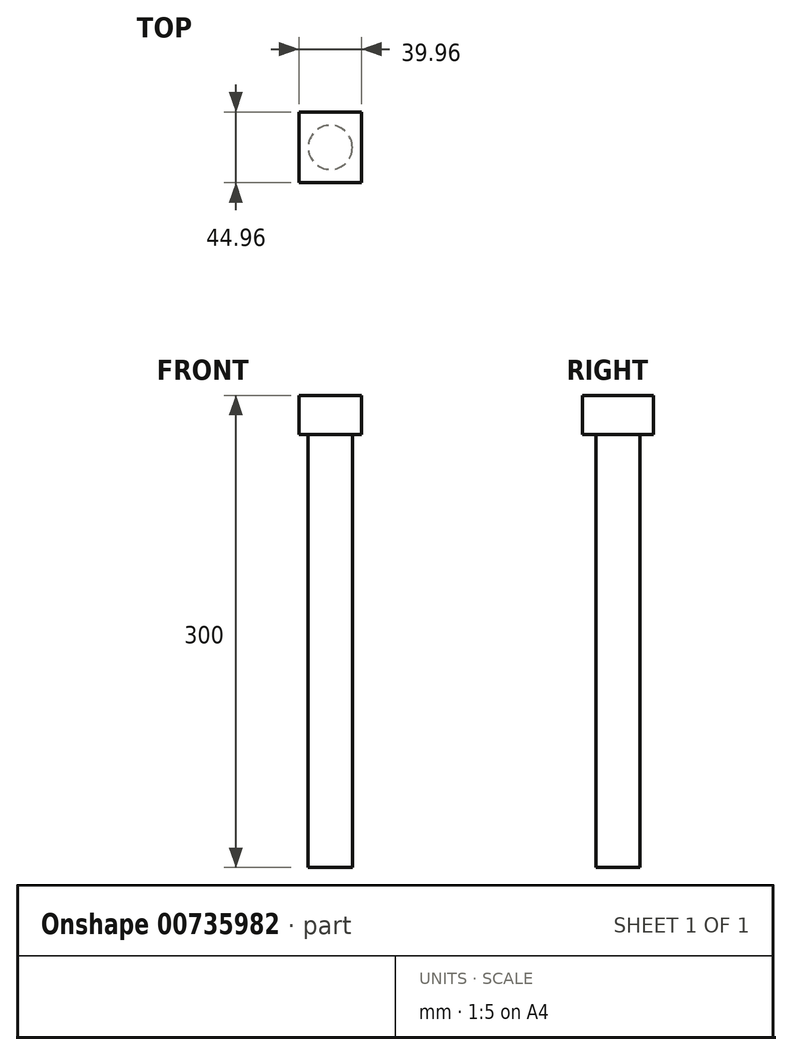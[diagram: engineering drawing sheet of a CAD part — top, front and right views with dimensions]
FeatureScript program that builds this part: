
annotation { "Feature Type Name" : "Feature", "Feature Type Description" : "" }
export const myFeature = defineFeature(function(context is Context, id is Id, definition is map)
    precondition{}
    {
        {
            var Q0;
            Q0=qCreatedBy(makeId("Top.planeOp"),FACE);
            var sketch = newSketch(context, id + "F0", { "sketchPlane" : qUnion([Q0])});
            skCircle(sketch, "E0", {"center": v(0, 0) * mm, "radius": 14 * mm});
            skSolve(sketch);
        }
        {
            var Q0;
            Q0 = qSketchRegion(id + "F0", true);
            extrude(context, id + "F1", {"entities" : qUnion([Q0]), "depth" : 300 * mm, "offsetDistance" : 25 * mm});
        }
        {
            var Q0;
            Q0=makeQuery(id+"F1.opExtrude","CAP_FACE",FACE,{"disambiguationData":[OSD([sQuery(id+"F0.wireOp",EDGE,"E0")])],"isStart":false});
            var sketch = newSketch(context, id + "F2", { "sketchPlane" : qUnion([Q0])});
            skLineSegment(sketch, "E1.bottom", {"start": v(19.98, -22.48) * mm, "end": v(-19.98, -22.48) * mm});
            skLineSegment(sketch, "E1.top", {"start": v(19.98, 22.48) * mm, "end": v(-19.98, 22.48) * mm});
            skLineSegment(sketch, "E1.left", {"start": v(19.98, -22.48) * mm, "end": v(19.98, 22.48) * mm});
            skLineSegment(sketch, "E1.right", {"start": v(-19.98, -22.48) * mm, "end": v(-19.98, 22.48) * mm});
            skPoint(sketch, "E1.middle", {"position": v(0, 0) * mm});
            skSolve(sketch);
        }
        {
            var Q0;
            Q0=makeQuery(id+"F2.imprint","IMPRINT",FACE,{"disambiguationData":[TD([[makeQuery(id+"F2.imprint","IMPRINT",EDGE,{"derivedFrom":sQuery(id+"F2.wireOp",EDGE,"E1.bottom")}),-1.0]])]});
            extrude(context, id + "F3", {"entities" : qUnion([Q0]), "operationType" : NewBodyOperationType.ADD, "oppositeDirection" : true, "depth" : 25 * mm, "offsetDistance" : 25 * mm});
        }
    });
